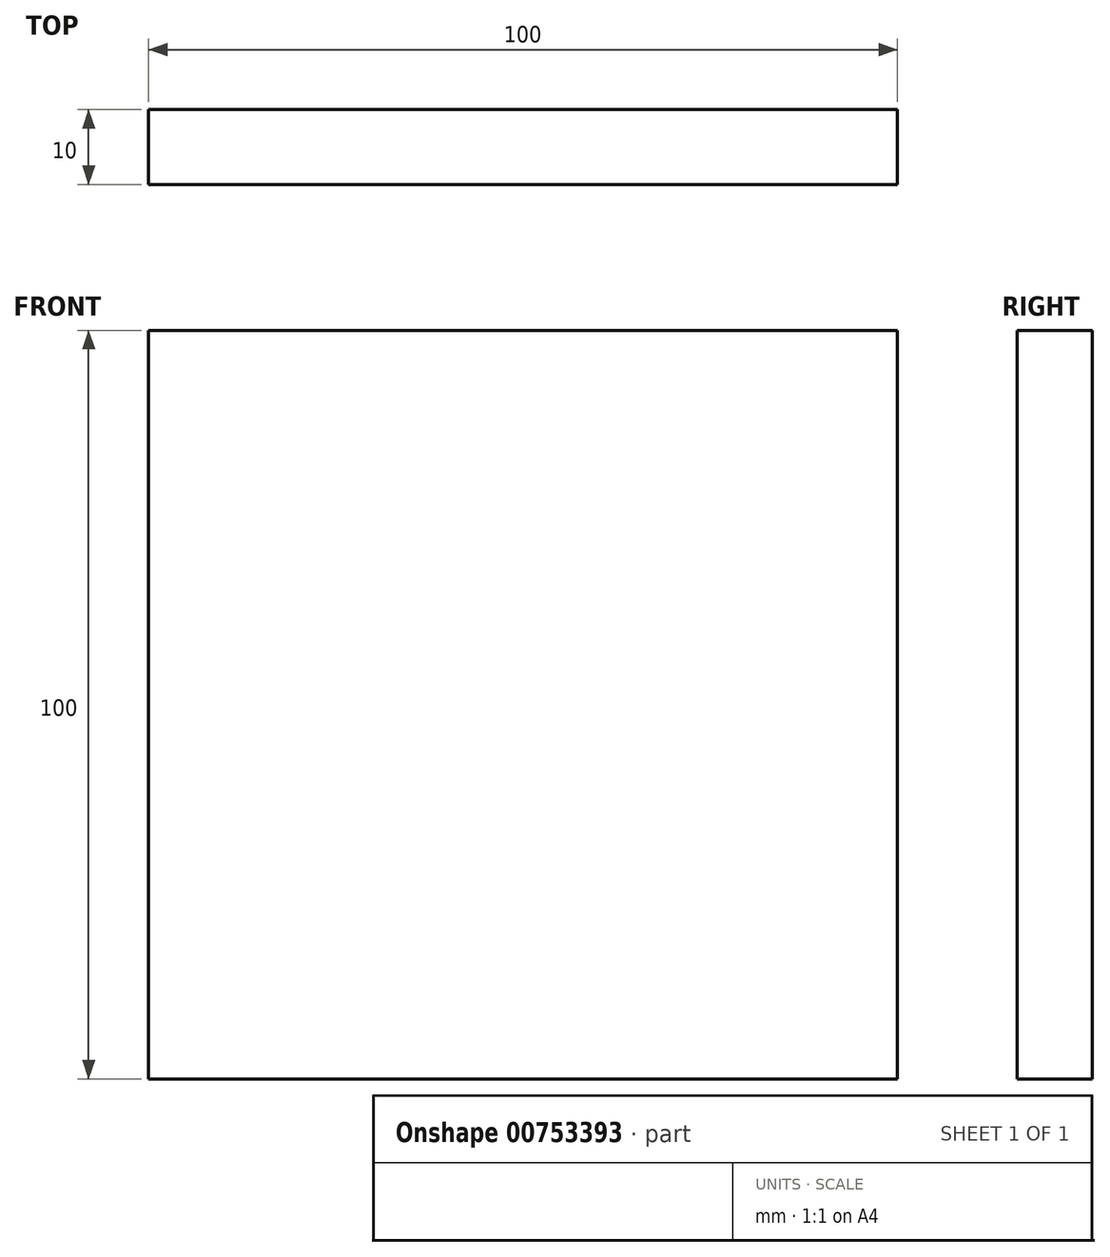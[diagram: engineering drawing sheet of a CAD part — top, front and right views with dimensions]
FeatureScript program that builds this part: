
annotation { "Feature Type Name" : "Feature", "Feature Type Description" : "" }
export const myFeature = defineFeature(function(context is Context, id is Id, definition is map)
    precondition{}
    {
        {
            var Q0;
            Q0=qCreatedBy(makeId("Front.planeOp"),FACE);
            var sketch = newSketch(context, id + "F0", { "sketchPlane" : qUnion([Q0])});
            skLineSegment(sketch, "E0.bottom", {"start": v(0, 0) * mm, "end": v(100, 0) * mm});
            skLineSegment(sketch, "E0.top", {"start": v(0, 100) * mm, "end": v(100, 100) * mm});
            skLineSegment(sketch, "E0.left", {"start": v(0, 0) * mm, "end": v(0, 100) * mm});
            skLineSegment(sketch, "E0.right", {"start": v(100, 0) * mm, "end": v(100, 100) * mm});
            skSolve(sketch);
        }
        {
            var Q0;
            Q0 = qSketchRegion(id + "F0", true);
            extrude(context, id + "F1", {"entities" : qUnion([Q0]), "depth" : 10 * mm, "offsetDistance" : 25 * mm});
        }
    });
